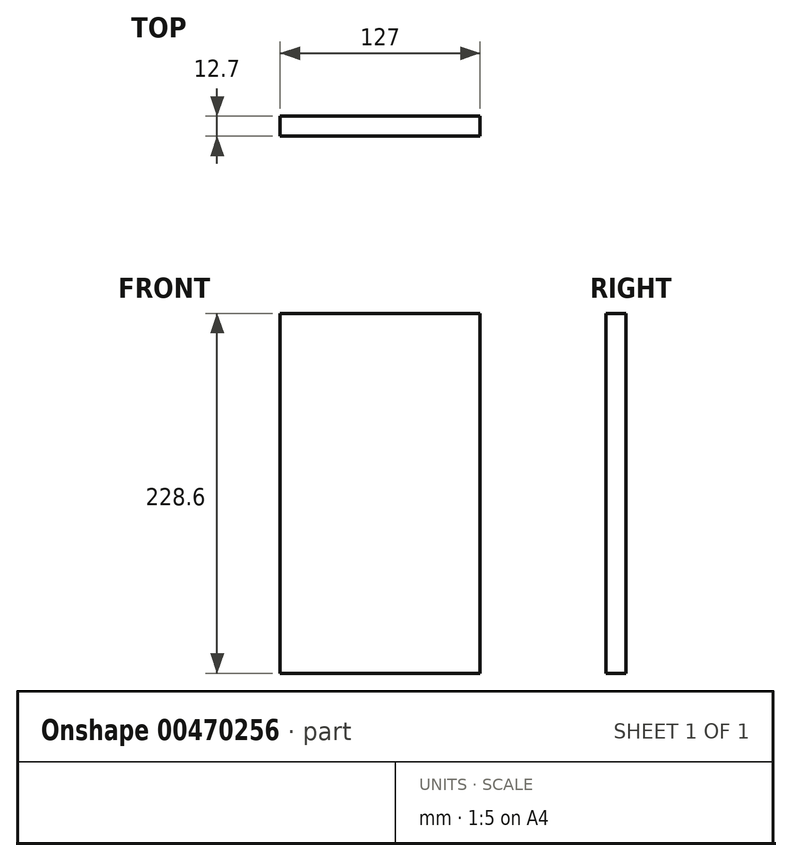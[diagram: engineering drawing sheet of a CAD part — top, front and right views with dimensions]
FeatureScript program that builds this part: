
annotation { "Feature Type Name" : "Feature", "Feature Type Description" : "" }
export const myFeature = defineFeature(function(context is Context, id is Id, definition is map)
    precondition{}
    {
        {
            var Q0;
            Q0=qCreatedBy(makeId("Front.planeOp"),FACE);
            var sketch = newSketch(context, id + "F0", { "sketchPlane" : qUnion([Q0])});
            skLineSegment(sketch, "E0.bottom", {"start": v(-64.62, 207.13) * mm, "end": v(62.38, 207.13) * mm});
            skLineSegment(sketch, "E0.top", {"start": v(-64.62, -21.47) * mm, "end": v(62.38, -21.47) * mm});
            skLineSegment(sketch, "E0.left", {"start": v(-64.62, 207.13) * mm, "end": v(-64.62, -21.47) * mm});
            skLineSegment(sketch, "E0.right", {"start": v(62.38, 207.13) * mm, "end": v(62.38, -21.47) * mm});
            skSolve(sketch);
        }
        {
            var Q0;
            Q0=makeQuery(id+"F0.imprint","IMPRINT",FACE,{"disambiguationData":[TD([[makeQuery(id+"F0.imprint","IMPRINT",EDGE,{"derivedFrom":sQuery(id+"F0.wireOp",EDGE,"E0.bottom")}),-1.0]])]});
            extrude(context, id + "F1", {"entities" : qUnion([Q0]), "depth" : 12.7 * mm});
        }
    });
